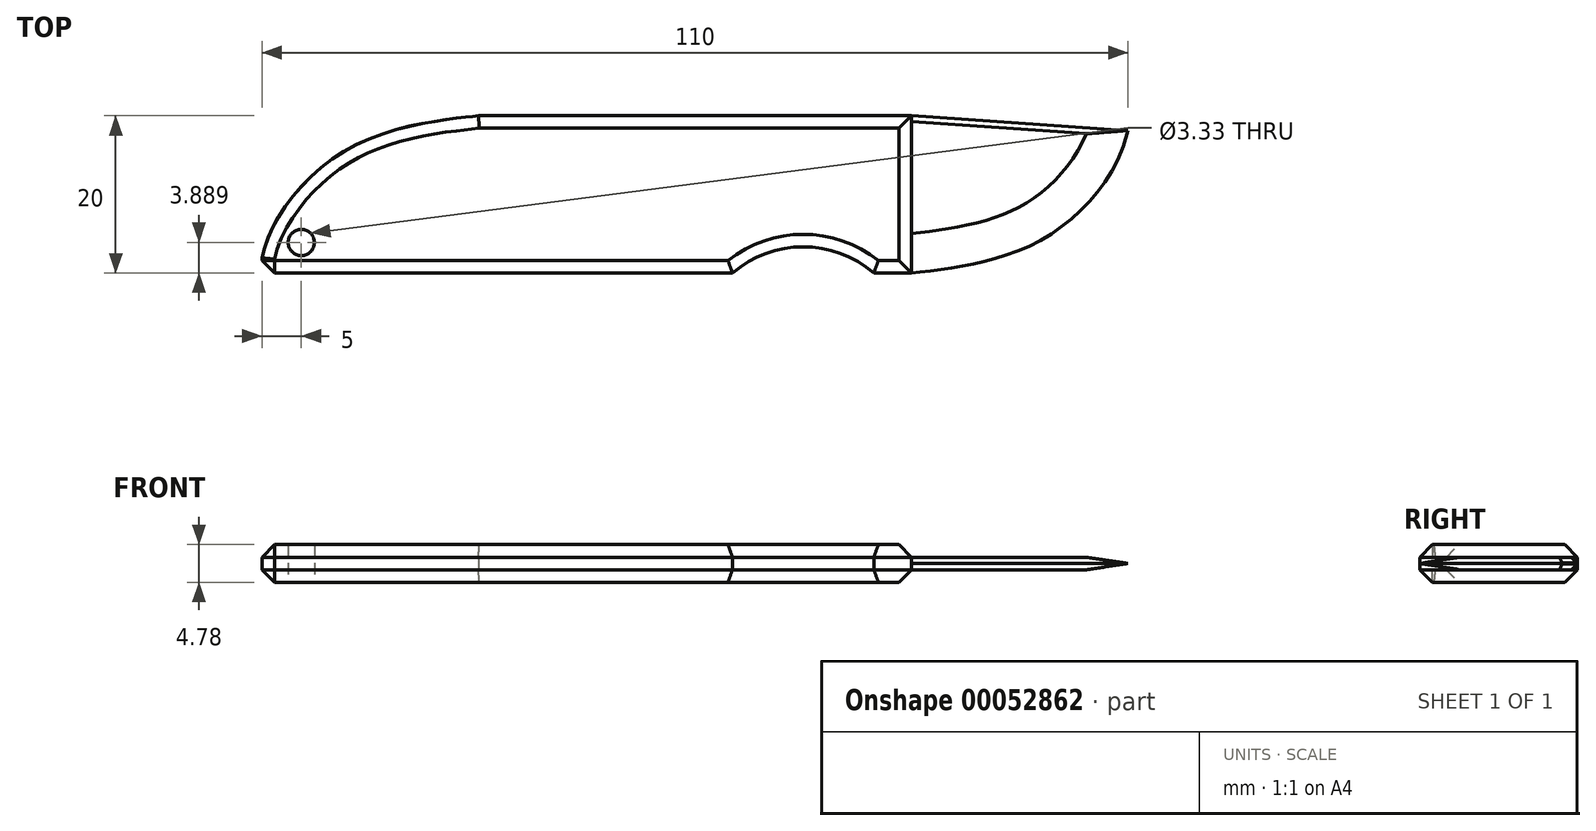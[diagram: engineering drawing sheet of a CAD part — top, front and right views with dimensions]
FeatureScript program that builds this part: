
annotation { "Feature Type Name" : "Feature", "Feature Type Description" : "" }
export const myFeature = defineFeature(function(context is Context, id is Id, definition is map)
    precondition{}
    {
        {
            assignVariable(context, id + "F0", {"name" : "width", "anyValue" : 20});
        }
        {
            var Q0;
            Q0=qCreatedBy(makeId("Top.planeOp"),FACE);
            var sketch = newSketch(context, id + "F1", { "sketchPlane" : qUnion([Q0])});
            skLineSegment(sketch, "E0", {"start": v(110, 0) * mm, "end": v(110, 20) * mm});
            skLineSegment(sketch, "E1", {"start": v(110, 20) * mm, "end": v(0, 20) * mm});
            skLineSegment(sketch, "E2", {"start": v(0, 20) * mm, "end": v(0, 0) * mm});
            skCircle(sketch, "E3", {"center": v(68.75, -10.42) * mm, "radius": 13.75 * mm});
            skLineSegment(sketch, "E4", {"start": v(82.5, 0) * mm, "end": v(82.5, 20) * mm});
            skLineSegment(sketch, "E5", {"start": v(55, 20) * mm, "end": v(55, 0) * mm, "construction": true});
            skLineSegment(sketch, "E6", {"start": v(0, 0) * mm, "end": v(55, 0) * mm});
            skLineSegment(sketch, "E7", {"start": v(55, 0) * mm, "end": v(82.5, 0) * mm});
            skLineSegment(sketch, "E8", {"start": v(82.5, 0) * mm, "end": v(110, 0) * mm});
            skPoint(sketch, "E9", {"position": v(68.75, 0) * mm});
            skLineSegment(sketch, "E10", {"start": v(82.5, 20) * mm, "end": v(110, 18.08) * mm});
            skFitSpline(sketch, "E11", {"points": [v(82.5, 0) * mm, v(98.19, 3.78) * mm, v(110, 18.08) * mm], "startDerivative": vector(13.57, 1.93) * mm, "endDerivative": vector(5.37, 28.1) * mm});
            skLineSegment(sketch, "E12", {"start": v(0, 10) * mm, "end": v(110, 10) * mm, "construction": true});
            skPoint(sketch, "E13.visualSharp", {"position": v(0, 0) * mm});
            skPoint(sketch, "E14.visualSharp", {"position": v(0, 20) * mm});
            skFitSpline(sketch, "E15.MirrorCS", {"points": [v(27.5, 0) * mm, v(11.81, 3.78) * mm, v(0, 18.08) * mm], "startDerivative": vector(-13.57, 1.93) * mm, "endDerivative": vector(-5.37, 28.1) * mm, "construction": true});
            skFitSpline(sketch, "E16.MirrorCS", {"points": [v(27.5, 20) * mm, v(11.81, 16.22) * mm, v(0, 1.92) * mm], "startDerivative": vector(-13.57, -1.93) * mm, "endDerivative": vector(-5.37, -28.1) * mm});
            skCircle(sketch, "E17", {"center": v(5, 3.89) * mm, "radius": 1.67 * mm});
            skSolve(sketch);
        }
        {
            assignVariable(context, id + "F2", {"name" : "bladeThickness", "anyValue" : 1.59});
        }
        {
            var Q0;
            Q0=makeQuery(id+"F1.imprint","IMPRINT",FACE,{"disambiguationData":[TD([[makeQuery(id+"F1.imprint","IMPRINT",EDGE,{"derivedFrom":sQuery(id+"F1.wireOp",EDGE,"E4")}),-1.0]])]});
            extrude(context, id + "F3", {"entities" : qUnion([Q0]), "endBound" : BoundingType.SYMMETRIC, "depth" : (getVariable(context, 'bladeThickness')) * mm});
        }
        {
            var Q0;
            Q0=makeQuery(id+"F3.opExtrude","CAP_EDGE",EDGE,{"disambiguationData":[OSD([sQuery(id+"F1.wireOp",EDGE,"E11")])],"isStart":false});
            var Q1;
            Q1=makeQuery(id+"F3.opExtrude","CAP_EDGE",EDGE,{"disambiguationData":[OSD([sQuery(id+"F1.wireOp",EDGE,"E11")])],"isStart":true});
            chamfer(context, id + "F4", {"entities" : qUnion([Q0, Q1]), "chamferType" : ChamferType.TWO_OFFSETS, "width1" : (getVariable(context, 'width') / 4) * mm, "oppositeDirection" : false, "width2" : (getVariable(context, 'bladeThickness') / 2) * mm});
        }
        {
            var Q0;
            Q0=makeQuery(id+"F3.opExtrude","CAP_EDGE",EDGE,{"disambiguationData":[OSD([sQuery(id+"F1.wireOp",EDGE,"E10")])],"isStart":false});
            var Q1;
            Q1=makeQuery(id+"F3.opExtrude","CAP_EDGE",EDGE,{"disambiguationData":[OSD([sQuery(id+"F1.wireOp",EDGE,"E10")])],"isStart":true});
            chamfer(context, id + "F5", {"entities" : qUnion([Q0, Q1]), "width" : .75 * mm, "tangentPropagation" : true});
        }
        {
            assignVariable(context, id + "F6", {"name" : "handleThickness", "anyValue" : getVariable(context, 'bladeThickness') * 3});
        }
        {
            var Q0;
            {var subQ3=sQuery(id+"F1.wireOp",EDGE,"b49e259a-454d-4176-9086-fcf70b9a0c15");Q0=makeQuery(id+"F1.imprint","IMPRINT",FACE,{"disambiguationData":[TD([[makeQuery(id+"F1.imprint","IMPRINT",EDGE,{"derivedFrom":subQ3}),1.0]])]});}
            var Q1;
            {var subQ0=sQuery(id+"F1.wireOp",EDGE,"E4");Q1=makeQuery(id+"F1.imprint","IMPRINT",FACE,{"disambiguationData":[TD([[makeQuery(id+"F1.imprint","IMPRINT",EDGE,{"derivedFrom":subQ0}),1.0]])]});}
            extrude(context, id + "F7", {"entities" : qUnion([Q0, Q1]), "operationType" : NewBodyOperationType.ADD, "endBound" : BoundingType.SYMMETRIC, "depth" : (getVariable(context, 'handleThickness')) * mm});
        }
        {
            var Q0;
            Q0=makeQuery(id+"F7.opExtrude","CAP_EDGE",EDGE,{"disambiguationData":[OSD([sQuery(id+"F1.wireOp",EDGE,"E4")])],"isStart":false});
            var Q1;
            Q1=makeQuery(id+"F7.opExtrude","CAP_EDGE",EDGE,{"disambiguationData":[OSD([sQuery(id+"F1.wireOp",EDGE,"E4")])],"isStart":true});
            var Q2;
            Q2=makeQuery(id+"F7.opExtrude","CAP_EDGE",EDGE,{"disambiguationData":[OSD([sQuery(id+"F1.wireOp",EDGE,"E2")])],"isStart":false});
            var Q3;
            Q3=makeQuery(id+"F7.opExtrude","CAP_EDGE",EDGE,{"disambiguationData":[OSD([sQuery(id+"F1.wireOp",EDGE,"E2")])],"isStart":true});
            var Q4;
            Q4=makeQuery(id+"F7.opExtrude","CAP_EDGE",EDGE,{"disambiguationData":[OSD([sQuery(id+"F1.wireOp",EDGE,"E3")])],"isStart":false});
            var Q5;
            Q5=makeQuery(id+"F7.opExtrude","CAP_EDGE",EDGE,{"disambiguationData":[OSD([sQuery(id+"F1.wireOp",EDGE,"E3")])],"isStart":true});
            var Q6;
            Q6=makeQuery(id+"F7.opExtrude","CAP_EDGE",EDGE,{"disambiguationData":[OSD([sQuery(id+"F1.wireOp",EDGE,"E7")])],"isStart":false});
            var Q7;
            Q7=makeQuery(id+"F7.opExtrude","CAP_EDGE",EDGE,{"disambiguationData":[OSD([sQuery(id+"F1.wireOp",EDGE,"E7")])],"isStart":true});
            var Q8;
            Q8=makeQuery(id+"F7.opExtrude","CAP_EDGE",EDGE,{"disambiguationData":[OSD([sQuery(id+"F1.wireOp",EDGE,"E16.MirrorCS")])],"isStart":false});
            var Q9;
            Q9=makeQuery(id+"F7.opExtrude","CAP_EDGE",EDGE,{"disambiguationData":[OSD([sQuery(id+"F1.wireOp",EDGE,"E16.MirrorCS")])],"isStart":true});
            var Q10;
            Q10=makeQuery(id+"F7.opExtrude","CAP_EDGE",EDGE,{"disambiguationData":[OSD([sQuery(id+"F1.wireOp",EDGE,"E1")])],"isStart":false});
            var Q11;
            Q11=makeQuery(id+"F7.opExtrude","CAP_EDGE",EDGE,{"disambiguationData":[OSD([sQuery(id+"F1.wireOp",EDGE,"E1")])],"isStart":true});
            var Q12;
            Q12=makeQuery(id+"F7.opExtrude","CAP_EDGE",EDGE,{"disambiguationData":[OSD([sQuery(id+"F1.wireOp",EDGE,"E6"),sQuery(id+"F1.wireOp",EDGE,"E7")])],"isStart":false});
            var Q13;
            Q13=makeQuery(id+"F7.opExtrude","CAP_EDGE",EDGE,{"disambiguationData":[OSD([sQuery(id+"F1.wireOp",EDGE,"E6"),sQuery(id+"F1.wireOp",EDGE,"E7")])],"isStart":true});
            var Q14;
            Q14=makeQuery(id+"F7.opExtrude","SWEPT_EDGE",EDGE,{"disambiguationData":[OSD([sQuery(id+"F1.wireOp",EDGE,"E2"),sQuery(id+"F1.wireOp",EDGE,"E6")])]});
            chamfer(context, id + "F8", {"entities" : qUnion([Q0, Q1, Q2, Q3, Q4, Q5, Q6, Q7, Q8, Q9, Q10, Q11, Q12, Q13, Q14]), "width" : (getVariable(context, 'handleThickness') / 3) * mm, "tangentPropagation" : true});
        }
    });
